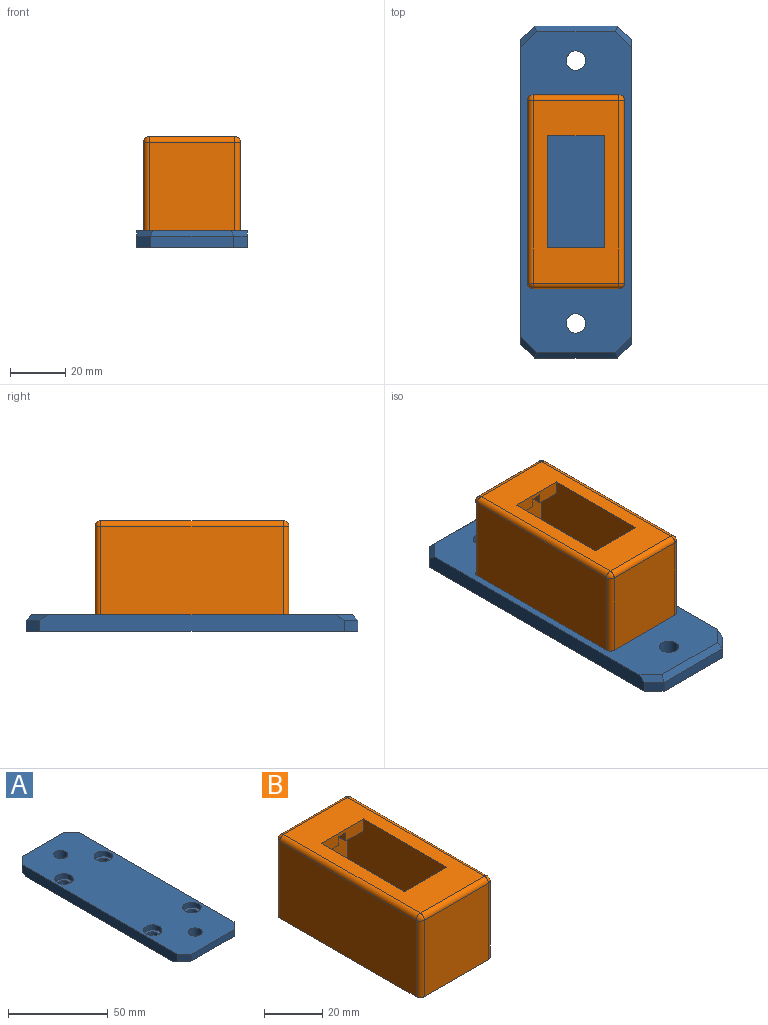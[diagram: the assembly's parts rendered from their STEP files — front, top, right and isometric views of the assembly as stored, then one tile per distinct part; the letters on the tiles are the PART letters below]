
ASSEMBLY  parts=2 mates=1
PART A: 30 faces, bbox 40x120x6 mm
  f0: plane 110x6mm, normal (1,0,0), area 654.3mm2, adj f4,f5,f20,f23,f24,f29
  f1: plane 30x4mm, normal (0,1,0), area 120mm2, adj f4,f22,f23,f28
  f2: plane 110x6mm, normal (-1,0,0), area 654.3mm2, adj f4,f5,f21,f22,f26,f27
  f3: plane 30x4mm, normal (0,-1,0), area 120mm2, adj f4,f20,f21,f25
  f4: plane 120x40mm, normal (0,0,1), area 4407.1mm2, adj f0,f1,f2,f3,f8,f11,f14,f17
  f5: plane 116x40mm, normal (0,0,-1), area 4400.1mm2, adj f0,f2,f6,f9,f12,f15,f18,f19
  f6: cylinder r=2.75mm len=5.5mm, axis (0,0,1), area 51.8mm2, adj f5,f7
  f7: plane 9.2x9.2mm, normal (0,0,1), area 42.7mm2, adj f6,f8
  f8: cylinder r=4.6mm len=9.2mm, axis (0,0,1), area 86.7mm2, adj f4,f7
  f9: cylinder r=2.75mm len=5.5mm, axis (0,0,1), area 51.8mm2, adj f5,f10
  f10: plane 9.2x9.2mm, normal (0,0,1), area 42.7mm2, adj f9,f11
  f11: cylinder r=4.6mm len=9.2mm, axis (0,0,1), area 86.7mm2, adj f4,f10
  f12: cylinder r=2.75mm len=5.5mm, axis (0,0,1), area 51.8mm2, adj f5,f13
  f13: plane 9.2x9.2mm, normal (0,0,1), area 42.7mm2, adj f12,f14
  f14: cylinder r=4.6mm len=9.2mm, axis (0,0,1), area 86.7mm2, adj f4,f13
  f15: cylinder r=2.75mm len=5.5mm, axis (0,0,1), area 51.8mm2, adj f5,f16
  f16: plane 9.2x9.2mm, normal (0,0,1), area 42.7mm2, adj f15,f17
  f17: cylinder r=4.6mm len=9.2mm, axis (0,0,1), area 86.7mm2, adj f4,f16
  f18: cylinder r=3.5mm len=7mm, axis (0,0,1), area 131.9mm2, adj f4,f5
  f19: cylinder r=3.5mm len=7mm, axis (0,0,1), area 131.9mm2, adj f4,f5
  f20: plane 5x5mm, normal (0.71,-0.71,0), area 28.3mm2, adj f0,f3,f4,f24
  f21: plane 5x5mm, normal (-0.71,-0.71,0), area 28.3mm2, adj f2,f3,f4,f26
  f22: plane 5x5mm, normal (-0.71,0.71,0), area 28.3mm2, adj f1,f2,f4,f27
  f23: plane 5x5mm, normal (0.71,0.71,0), area 28.3mm2, adj f0,f1,f4,f29
  f24: plane 7.83x5.83mm, normal (0.5,-0.5,-0.71), area 21.7mm2, adj f0,f5,f20,f25
  f25: plane 30x2mm, normal (0,-0.71,-0.71), area 82.5mm2, adj f3,f5,f24,f26
  f26: plane 7.83x5.83mm, normal (-0.5,-0.5,-0.71), area 21.7mm2, adj f2,f5,f21,f25
  f27: plane 7.83x5.83mm, normal (-0.5,0.5,-0.71), area 21.7mm2, adj f2,f5,f22,f28
  f28: plane 30x2mm, normal (0,0.71,-0.71), area 82.5mm2, adj f1,f5,f27,f29
  f29: plane 7.83x5.83mm, normal (0.5,0.5,-0.71), area 21.7mm2, adj f0,f5,f23,f28
PART B: 45 faces, bbox 35x70x34 mm
  f0: plane 29x20.5mm, normal (0,-1,0), area 540.5mm2, adj f1,f9,f11,f13,f42,f43,f44
  f1: plane 20.5x7.55mm, normal (0,0,-1), area 133.8mm2, adj f0,f2,f9,f11,f18,f19,f20
  f2: plane 20.5x5mm, normal (0,-1,0), area 90.2mm2, adj f1,f8,f9,f11,f19,f20,f21
  f3: plane 20.5x7.55mm, normal (0,0,-1), area 133.8mm2, adj f9,f10,f11,f12,f14,f15,f16
  f4: plane 32x31mm, normal (0,-1,0), area 992mm2, adj f13,f32,f38,f41
  f5: plane 66x32mm, normal (1,0,0), area 2112mm2, adj f13,f35,f39,f41
  f6: plane 32x31mm, normal (0,1,0), area 938mm2, adj f13,f30,f34,f35,f42,f43,f44
  f7: plane 66x32mm, normal (-1,0,0), area 2112mm2, adj f13,f30,f32,f33
  f8: plane 66x31mm, normal (0,0,1), area 1215.7mm2, adj f2,f9,f11,f12,f33,f34,f38,f39
  f9: plane 55.6x34mm, normal (-1,0,0), area 1814.9mm2, adj f0,f1,f2,f3,f8,f10,f12,f13
  f10: plane 29x20.5mm, normal (0,1,0), area 594.5mm2, adj f3,f9,f11,f13
  f11: plane 55.6x34mm, normal (1,0,0), area 1814.9mm2, adj f0,f1,f2,f3,f8,f10,f12,f13
  f12: plane 20.5x5mm, normal (0,1,0), area 90.2mm2, adj f3,f8,f9,f11,f15,f16,f17
  f13: plane 70x35mm, normal (0,0,-1), area 1186.5mm2, adj f0,f4,f5,f6,f7,f9,f10,f11
  f14: plane 3.5x3.5mm, normal (0,1,0), area 12.2mm2, adj f3,f15,f16,f17
  f15: plane 6x3.5mm, normal (1,0,0), area 21mm2, adj f3,f12,f14,f17
  f16: plane 6x3.5mm, normal (-1,0,0), area 21mm2, adj f3,f12,f14,f17
  f17: plane 6x3.5mm, normal (0,0,-1), area 21mm2, adj f12,f14,f15,f16
  f18: plane 3.5x3.5mm, normal (0,-1,0), area 12.2mm2, adj f1,f19,f20,f21
  f19: plane 6x3.5mm, normal (-1,0,0), area 21mm2, adj f1,f2,f18,f21
  f20: plane 6x3.5mm, normal (1,0,0), area 21mm2, adj f1,f2,f18,f21
  f21: plane 6x3.5mm, normal (0,0,-1), area 21mm2, adj f2,f18,f19,f20
  f22: cylinder r=2.1mm len=15mm, axis (0,0,-1), area 197.9mm2, adj f13,f23
  f23: cone r=0mm half-angle=59deg, axis (0,0,-1), area 16.2mm2, adj f22
  f24: cylinder r=2.1mm len=15mm, axis (0,0,-1), area 197.9mm2, adj f13,f25
  f25: cone r=0mm half-angle=59deg, axis (0,0,-1), area 16.2mm2, adj f24
  f26: cylinder r=2.1mm len=15mm, axis (0,0,-1), area 197.9mm2, adj f13,f27
  f27: cone r=0mm half-angle=59deg, axis (0,0,-1), area 16.2mm2, adj f26
  f28: cylinder r=2.1mm len=15mm, axis (0,0,-1), area 197.9mm2, adj f13,f29
  f29: cone r=0mm half-angle=59deg, axis (0,0,-1), area 16.2mm2, adj f28
  f30: cylinder r=2mm len=32mm, axis (0,0,-1), area 100.5mm2, adj f6,f7,f13,f31
  f31: sphere r=2mm, area 6.3mm2, adj f30,f33,f34
  f32: cylinder r=2mm len=32mm, axis (0,0,1), area 100.5mm2, adj f4,f7,f13,f36
  f33: cylinder r=2mm len=66mm, axis (0,1,0), area 207.3mm2, adj f7,f8,f31,f36
  f34: cylinder r=2mm len=31mm, axis (1,0,0), area 97.4mm2, adj f6,f8,f31,f37
  f35: cylinder r=2mm len=32mm, axis (0,0,1), area 100.5mm2, adj f5,f6,f13,f37
  f36: sphere r=2mm, area 6.3mm2, adj f32,f33,f38
  f37: sphere r=2mm, area 6.3mm2, adj f34,f35,f39
  f38: cylinder r=2mm len=31mm, axis (-1,0,0), area 97.4mm2, adj f4,f8,f36,f40
  f39: cylinder r=2mm len=66mm, axis (0,-1,0), area 207.3mm2, adj f5,f8,f37,f40
  f40: sphere r=2mm, area 6.3mm2, adj f38,f39,f41
  f41: cylinder r=2mm len=32mm, axis (0,0,-1), area 100.5mm2, adj f4,f5,f13,f40
  f42: plane 7.2x6mm, normal (1,0,0), area 43.2mm2, adj f0,f6,f13,f43
  f43: plane 9x7.2mm, normal (0,0,-1), area 64.8mm2, adj f0,f6,f42,f44
  f44: plane 7.2x6mm, normal (-1,0,0), area 43.2mm2, adj f0,f6,f13,f43
PLACE A rot(axis=(0,1,0),180deg) t=(-22.6,-2.15,-0.76)mm
PLACE B t=(-22.6,-2.15,-6.76)mm
MATE fastened A.f9 <-> B.f28  axis (0,0,1) through (-36.48,29.25,-0.76)mm
